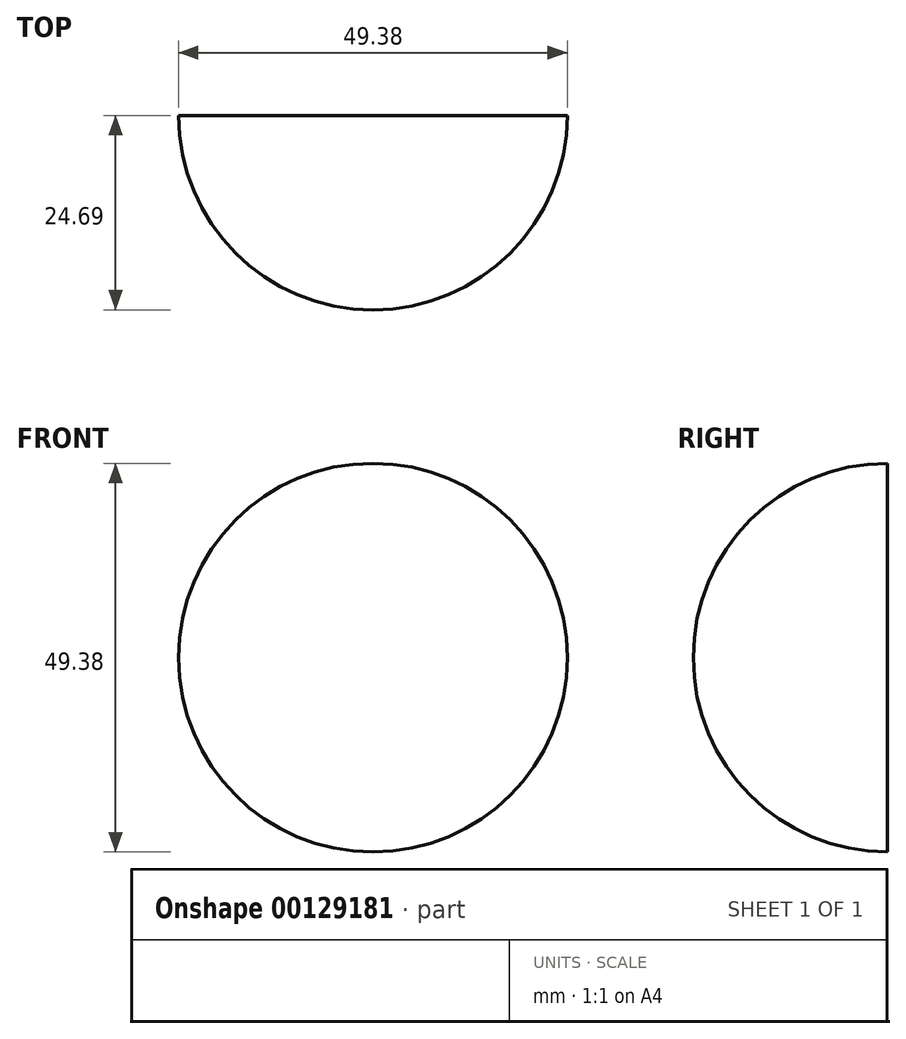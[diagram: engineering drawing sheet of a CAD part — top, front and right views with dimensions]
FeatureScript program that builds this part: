
annotation { "Feature Type Name" : "Feature", "Feature Type Description" : "" }
export const myFeature = defineFeature(function(context is Context, id is Id, definition is map)
    precondition{}
    {
        {
            var Q0;
            Q0=qCreatedBy(makeId("Front.planeOp"),FACE);
            var sketch = newSketch(context, id + "F0", { "sketchPlane" : qUnion([Q0])});
            skArc(sketch, "E0", {"start": v(0, -24.7) * mm, "mid": v(-24.7, 0) * mm, "end": v(0, 24.7) * mm});
            skLineSegment(sketch, "E1", {"start": v(0, -24.7) * mm, "end": v(0, 24.7) * mm, "construction": true});
            skSolve(sketch);
        }
        {
            var Q0;
            Q0=sQuery(id+"F0.wireOp",EDGE,"E0");
            var Q1;
            Q1=sQuery(id+"F0.wireOp",EDGE,"E1");
            revolve(context, id + "F1", {"bodyType" : ToolBodyType.SURFACE, "surfaceEntities" : qUnion([Q0]), "axis" : qUnion([Q1]), "revolveType" : RevolveType.ONE_DIRECTION, "angle" : 180 * degree});
        }
    });
